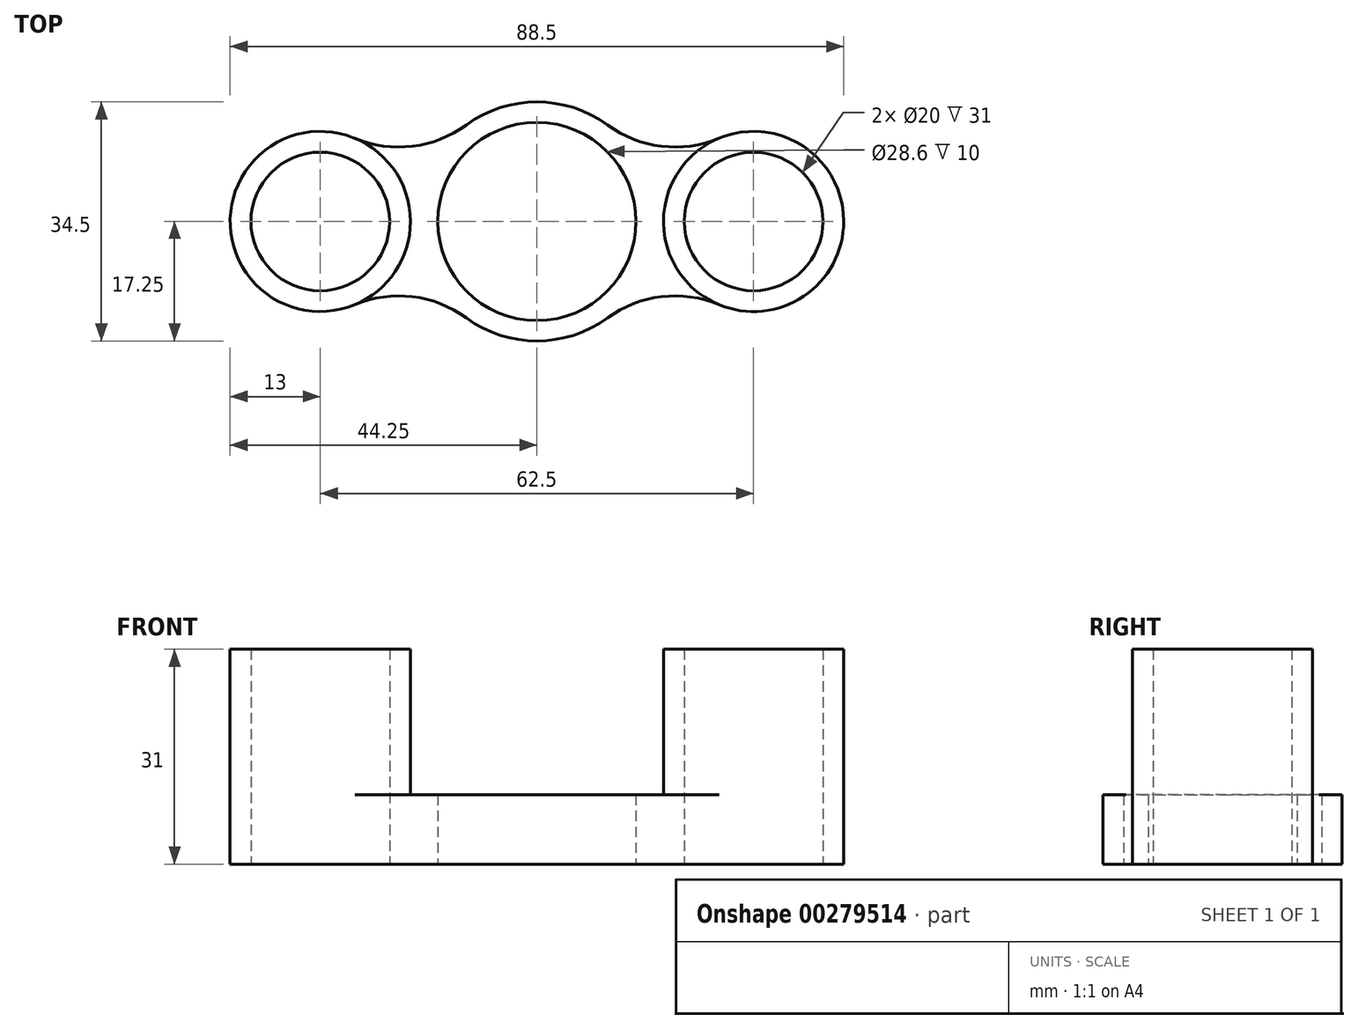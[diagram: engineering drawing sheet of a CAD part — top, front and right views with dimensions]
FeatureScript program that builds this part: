
annotation { "Feature Type Name" : "Feature", "Feature Type Description" : "" }
export const myFeature = defineFeature(function(context is Context, id is Id, definition is map)
    precondition{}
    {
        {
            var Q0;
            Q0=qCreatedBy(makeId("Top.planeOp"),FACE);
            var sketch = newSketch(context, id + "F0", { "sketchPlane" : qUnion([Q0])});
            skCircle(sketch, "E0", {"center": v(0, 0) * mm, "radius": 14.3 * mm, "construction": true});
            skCircle(sketch, "E1.0", {"center": v(0, 0) * mm, "radius": 17.25 * mm, "construction": true});
            skCircle(sketch, "E2", {"center": v(31.25, 0) * mm, "radius": 10 * mm, "construction": true});
            skCircle(sketch, "E3.0", {"center": v(31.25, 0) * mm, "radius": 13 * mm, "construction": true});
            skCircle(sketch, "E4.MirrorC", {"center": v(-31.25, 0) * mm, "radius": 13 * mm, "construction": true});
            skCircle(sketch, "E5.MirrorC", {"center": v(-31.25, 0) * mm, "radius": 10 * mm, "construction": true});
            skCircle(sketch, "E6", {"center": v(19.93, -27.24) * mm, "radius": 16.5 * mm, "construction": true});
            skCircle(sketch, "E7", {"center": v(19.93, 27.24) * mm, "radius": 16.5 * mm, "construction": true});
            skCircle(sketch, "E8.MirrorC", {"center": v(-19.93, 27.24) * mm, "radius": 16.5 * mm, "construction": true});
            skCircle(sketch, "E9.MirrorC", {"center": v(-19.93, -27.24) * mm, "radius": 16.5 * mm, "construction": true});
            skLineSegment(sketch, "E10.bottom", {"start": v(-44.25, 17.25) * mm, "end": v(44.25, 17.25) * mm, "construction": true});
            skLineSegment(sketch, "E10.top", {"start": v(-44.25, -17.25) * mm, "end": v(44.25, -17.25) * mm, "construction": true});
            skLineSegment(sketch, "E10.left", {"start": v(-44.25, 17.25) * mm, "end": v(-44.25, -17.25) * mm, "construction": true});
            skLineSegment(sketch, "E10.right", {"start": v(44.25, 17.25) * mm, "end": v(44.25, -17.25) * mm, "construction": true});
            skArc(sketch, "E11", {"start": v(-26.26, 12) * mm, "mid": v(-44.25, 0) * mm, "end": v(-26.26, -12) * mm});
            skArc(sketch, "E12", {"start": v(-26.26, -12) * mm, "mid": v(-17.97, -10.86) * mm, "end": v(-10.18, -13.92) * mm});
            skArc(sketch, "E13", {"start": v(-10.18, -13.92) * mm, "mid": v(-5.36, -16.4) * mm, "end": v(0, -17.25) * mm});
            skArc(sketch, "E14", {"start": v(-26.26, 12) * mm, "mid": v(-17.97, 10.86) * mm, "end": v(-10.18, 13.92) * mm});
            skArc(sketch, "E15", {"start": v(-10.18, 13.92) * mm, "mid": v(-5.36, 16.4) * mm, "end": v(0, 17.25) * mm});
            skArc(sketch, "E16.MirrorCS", {"start": v(10.18, 13.92) * mm, "mid": v(5.36, 16.4) * mm, "end": v(0, 17.25) * mm, "construction": true});
            skArc(sketch, "E17.MirrorCS", {"start": v(26.26, 12) * mm, "mid": v(17.97, 10.86) * mm, "end": v(10.18, 13.92) * mm});
            skArc(sketch, "E18.MirrorCS", {"start": v(26.26, 12) * mm, "mid": v(44.25, 0) * mm, "end": v(26.26, -12) * mm});
            skArc(sketch, "E19.MirrorCS", {"start": v(26.26, -12) * mm, "mid": v(17.97, -10.86) * mm, "end": v(10.18, -13.92) * mm});
            skArc(sketch, "E20.MirrorCS", {"start": v(10.18, -13.92) * mm, "mid": v(5.36, -16.4) * mm, "end": v(0, -17.25) * mm});
            skArc(sketch, "E21.MirrorCS", {"start": v(10.18, 13.92) * mm, "mid": v(5.36, 16.4) * mm, "end": v(0, 17.25) * mm});
            skSolve(sketch);
        }
        {
            var Q0;
            Q0 = qSketchRegion(id + "F0", true);
            extrude(context, id + "F1", {"entities" : qUnion([Q0]), "depth" : 31 * mm});
        }
        {
            var Q0;
            Q0=qCreatedBy(makeId("Top.planeOp"),FACE);
            var sketch = newSketch(context, id + "F2", { "sketchPlane" : qUnion([Q0])});
            skCircle(sketch, "E22.0", {"center": v(0, 0) * mm, "radius": 17.25 * mm, "construction": true});
            skCircle(sketch, "E23.0", {"center": v(31.25, 0) * mm, "radius": 13 * mm, "construction": true});
            skCircle(sketch, "E24.0", {"center": v(19.93, 27.24) * mm, "radius": 16.5 * mm, "construction": true});
            skCircle(sketch, "E25.0", {"center": v(-19.93, 27.24) * mm, "radius": 16.5 * mm, "construction": true});
            skCircle(sketch, "E26.0", {"center": v(-31.25, 0) * mm, "radius": 13 * mm, "construction": true});
            skCircle(sketch, "E27.0", {"center": v(-19.93, -27.24) * mm, "radius": 16.5 * mm, "construction": true});
            skCircle(sketch, "E28.0", {"center": v(19.93, -27.24) * mm, "radius": 16.5 * mm, "construction": true});
            skCircle(sketch, "E29.0", {"center": v(0, 0) * mm, "radius": 14.3 * mm});
            skCircle(sketch, "E30.0", {"center": v(-31.25, 0) * mm, "radius": 10 * mm});
            skCircle(sketch, "E31.0", {"center": v(31.25, 0) * mm, "radius": 10 * mm});
            skSolve(sketch);
        }
        {
            var Q0;
            Q0 = qSketchRegion(id + "F2", true);
            extrude(context, id + "F3", {"entities" : qUnion([Q0]), "operationType" : NewBodyOperationType.REMOVE, "endBound" : BoundingType.THROUGH_ALL, "depth" : 25 * mm});
        }
        {
            var Q0;
            Q0=makeQuery(id+"F1.opExtrude","CAP_FACE",FACE,{"disambiguationData":[OSD([sQuery(id+"F0.wireOp",EDGE,"E11"),sQuery(id+"F0.wireOp",EDGE,"E12"),sQuery(id+"F0.wireOp",EDGE,"E13"),sQuery(id+"F0.wireOp",EDGE,"E14"),sQuery(id+"F0.wireOp",EDGE,"E15"),sQuery(id+"F0.wireOp",EDGE,"E17.MirrorCS"),sQuery(id+"F0.wireOp",EDGE,"E18.MirrorCS"),sQuery(id+"F0.wireOp",EDGE,"E19.MirrorCS"),sQuery(id+"F0.wireOp",EDGE,"E20.MirrorCS"),sQuery(id+"F0.wireOp",EDGE,"E21.MirrorCS")])],"isStart":false});
            var sketch = newSketch(context, id + "F4", { "sketchPlane" : qUnion([Q0])});
            skLineSegment(sketch, "E32.bottom", {"start": v(-16.5, 40) * mm, "end": v(16.5, 40) * mm});
            skLineSegment(sketch, "E32.top", {"start": v(-16.5, -40) * mm, "end": v(16.5, -40) * mm});
            skLineSegment(sketch, "E32.left", {"start": v(-16.5, 40) * mm, "end": v(-16.5, -40) * mm});
            skLineSegment(sketch, "E32.right", {"start": v(16.5, 40) * mm, "end": v(16.5, -40) * mm});
            skLineSegment(sketch, "E33", {"start": v(0, 40) * mm, "end": v(0, -40) * mm, "construction": true});
            skSolve(sketch);
        }
        {
            var Q0;
            Q0 = qSketchRegion(id + "F4", true);
            extrude(context, id + "F5", {"entities" : qUnion([Q0]), "operationType" : NewBodyOperationType.REMOVE, "oppositeDirection" : true, "depth" : 21 * mm});
        }
        {
            var Q0;
            Q0=qCreatedBy(makeId("Top.planeOp"),FACE);
            var sketch = newSketch(context, id + "F6", { "sketchPlane" : qUnion([Q0])});
            skCircle(sketch, "E34.0", {"center": v(-31.25, 0) * mm, "radius": 13 * mm});
            skCircle(sketch, "E35.0", {"center": v(31.25, 0) * mm, "radius": 13 * mm});
            skCircle(sketch, "E36", {"center": v(-31.25, 0) * mm, "radius": 22.5 * mm});
            skCircle(sketch, "E37", {"center": v(31.25, 0) * mm, "radius": 22.5 * mm});
            skSolve(sketch);
        }
        {
            var Q0;
            Q0 = qSketchRegion(id + "F6", true);
            extrude(context, id + "F7", {"entities" : qUnion([Q0]), "operationType" : NewBodyOperationType.REMOVE, "endBound" : BoundingType.THROUGH_ALL, "depth" : 25 * mm, "hasSecondDirection" : true, "secondDirectionOppositeDirection" : false, "secondDirectionDepth" : 10 * mm});
        }
    });
